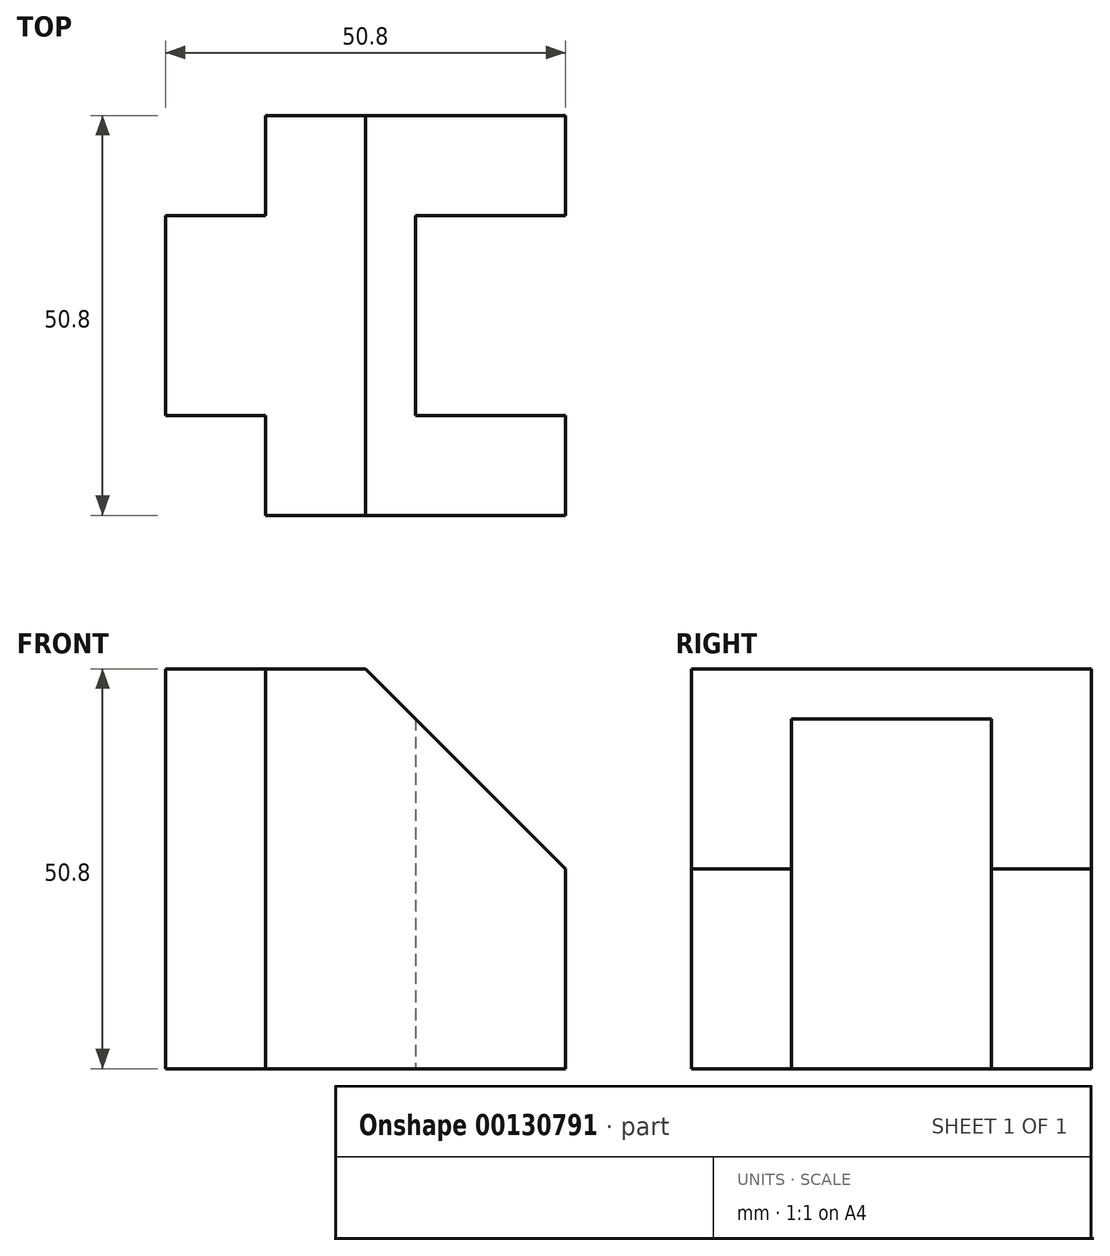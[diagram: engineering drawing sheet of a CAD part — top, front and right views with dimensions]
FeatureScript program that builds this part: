
annotation { "Feature Type Name" : "Feature", "Feature Type Description" : "" }
export const myFeature = defineFeature(function(context is Context, id is Id, definition is map)
    precondition{}
    {
        {
            var Q0;
            Q0=qCreatedBy(makeId("Front.planeOp"),FACE);
            var sketch = newSketch(context, id + "F0", { "sketchPlane" : qUnion([Q0])});
            skLineSegment(sketch, "E0.bottom", {"start": v(0, 0) * mm, "end": v(12.7, 0) * mm});
            skLineSegment(sketch, "E0.top", {"start": v(0, 50.8) * mm, "end": v(12.7, 50.8) * mm});
            skLineSegment(sketch, "E0.left", {"start": v(0, 0) * mm, "end": v(0, 50.8) * mm});
            skLineSegment(sketch, "E0.right", {"start": v(12.7, 0) * mm, "end": v(12.7, 50.8) * mm});
            skLineSegment(sketch, "E1", {"start": v(12.7, 50.8) * mm, "end": v(25.4, 50.8) * mm});
            skLineSegment(sketch, "E2", {"start": v(25.4, 50.8) * mm, "end": v(50.8, 25.4) * mm});
            skLineSegment(sketch, "E3", {"start": v(50.8, 25.4) * mm, "end": v(50.8, 0) * mm});
            skLineSegment(sketch, "E4", {"start": v(50.8, 0) * mm, "end": v(12.7, 0) * mm});
            skSolve(sketch);
        }
        {
            var Q0;
            Q0 = qSketchRegion(id + "F0", true);
            extrude(context, id + "F1", {"entities" : qUnion([Q0]), "oppositeDirection" : true, "depth" : 50.8 * mm});
        }
        {
            var Q0;
            Q0=makeQuery(id+"F1.opExtrude","SWEPT_FACE",FACE,{"disambiguationData":[OSD([sQuery(id+"F0.wireOp",EDGE,"E0.top"),sQuery(id+"F0.wireOp",EDGE,"E1")])]});
            var sketch = newSketch(context, id + "F2", { "sketchPlane" : qUnion([Q0])});
            skLineSegment(sketch, "E5", {"start": v(25.4, 0) * mm, "end": v(12.7, 0) * mm});
            skLineSegment(sketch, "E6", {"start": v(12.7, 0) * mm, "end": v(12.7, 12.7) * mm});
            skLineSegment(sketch, "E7", {"start": v(12.7, 12.7) * mm, "end": v(0, 12.7) * mm});
            skLineSegment(sketch, "E8", {"start": v(0, 12.7) * mm, "end": v(0, 38.1) * mm});
            skLineSegment(sketch, "E9", {"start": v(0, 38.1) * mm, "end": v(12.7, 38.1) * mm});
            skLineSegment(sketch, "E10", {"start": v(12.7, 38.1) * mm, "end": v(12.7, 50.8) * mm});
            skLineSegment(sketch, "E11", {"start": v(12.7, 50.8) * mm, "end": v(25.4, 50.8) * mm});
            skLineSegment(sketch, "E12", {"start": v(25.4, 50.8) * mm, "end": v(25.4, 0) * mm});
            skLineSegment(sketch, "E13", {"start": v(12.7, 0) * mm, "end": v(0, 0) * mm});
            skLineSegment(sketch, "E14", {"start": v(0, 0) * mm, "end": v(0, 12.7) * mm});
            skLineSegment(sketch, "E15", {"start": v(0, 38.1) * mm, "end": v(0, 50.8) * mm});
            skLineSegment(sketch, "E16", {"start": v(0, 50.8) * mm, "end": v(12.7, 50.8) * mm});
            skSolve(sketch);
        }
        {
            var Q0;
            Q0=makeQuery(id+"F2.imprint","IMPRINT",FACE,{"disambiguationData":[TD([[makeQuery(id+"F2.imprint","IMPRINT",EDGE,{"derivedFrom":sQuery(id+"F2.wireOp",EDGE,"E6")}),1.0]])]});
            var Q1;
            Q1=makeQuery(id+"F2.imprint","IMPRINT",FACE,{"disambiguationData":[TD([[makeQuery(id+"F2.imprint","IMPRINT",EDGE,{"derivedFrom":sQuery(id+"F2.wireOp",EDGE,"E9")}),1.0]])]});
            extrude(context, id + "F3", {"entities" : qUnion([Q0, Q1]), "operationType" : NewBodyOperationType.REMOVE, "oppositeDirection" : true, "depth" : 50.8 * mm});
        }
        {
            var Q0;
            Q0=qCreatedBy(makeId("Top.planeOp"),FACE);
            var sketch = newSketch(context, id + "F4", { "sketchPlane" : qUnion([Q0])});
            skLineSegment(sketch, "E17.bottom", {"start": v(50.8, 38.1) * mm, "end": v(31.75, 38.1) * mm});
            skLineSegment(sketch, "E17.top", {"start": v(50.8, 12.7) * mm, "end": v(31.75, 12.7) * mm});
            skLineSegment(sketch, "E17.left", {"start": v(50.8, 38.1) * mm, "end": v(50.8, 12.7) * mm});
            skLineSegment(sketch, "E17.right", {"start": v(31.75, 38.1) * mm, "end": v(31.75, 12.7) * mm});
            skLineSegment(sketch, "E18", {"start": v(25.4, 0) * mm, "end": v(25.4, 50.8) * mm, "construction": true});
            skLineSegment(sketch, "E19", {"start": v(25.4, 50.8) * mm, "end": v(50.8, 50.8) * mm, "construction": true});
            skLineSegment(sketch, "E20", {"start": v(50.8, 50.8) * mm, "end": v(50.8, 0) * mm, "construction": true});
            skLineSegment(sketch, "E21", {"start": v(50.8, 0) * mm, "end": v(25.4, 0) * mm, "construction": true});
            skSolve(sketch);
        }
        {
            var Q0;
            Q0 = qSketchRegion(id + "F4", true);
            extrude(context, id + "F5", {"entities" : qUnion([Q0]), "operationType" : NewBodyOperationType.REMOVE, "depth" : 50.8 * mm});
        }
    });
